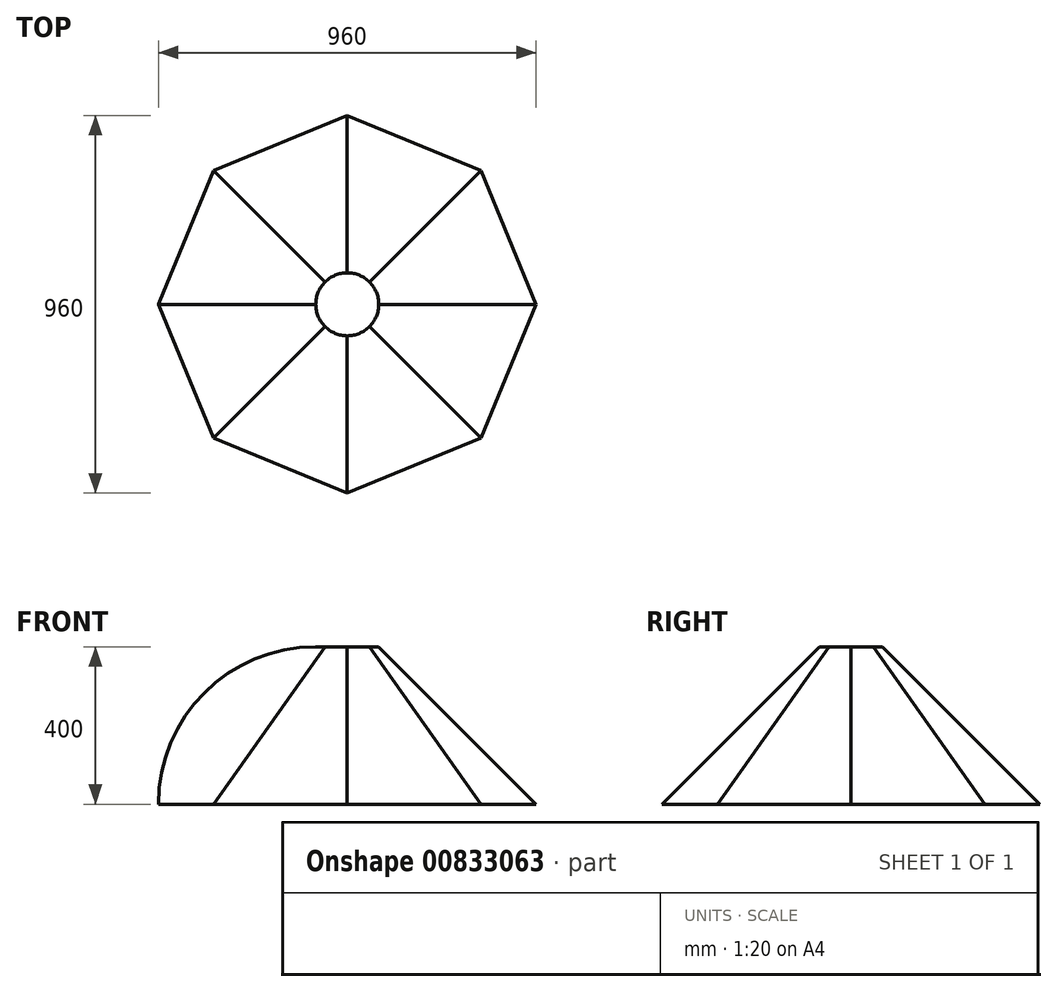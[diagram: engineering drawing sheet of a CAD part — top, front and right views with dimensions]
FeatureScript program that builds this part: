
annotation { "Feature Type Name" : "Feature", "Feature Type Description" : "" }
export const myFeature = defineFeature(function(context is Context, id is Id, definition is map)
    precondition{}
    {
        {
            var Q0;
            Q0=qCreatedBy(makeId("Top.planeOp"),FACE);
            cPlane(context, id + "F0", {"entities" : qUnion([Q0]), "cplaneType" : CPlaneType.OFFSET, "offset" : 400 * mm, "width" : 150 * mm, "height" : 150 * mm});
        }
        {
            var Q0;
            Q0=qCreatedBy(id+"F0.planeOp",FACE);
            var sketch = newSketch(context, id + "F1", { "sketchPlane" : qUnion([Q0])});
            skCircle(sketch, "E0", {"center": v(0, 0) * mm, "radius": 80 * mm});
            skSolve(sketch);
        }
        {
            var Q0;
            Q0=qCreatedBy(makeId("Top.planeOp"),FACE);
            var sketch = newSketch(context, id + "F2", { "sketchPlane" : qUnion([Q0])});
            skCircle(sketch, "E1.cCircle", {"center": v(0, 0) * mm, "radius": 443.46 * mm, "construction": true});
            skLineSegment(sketch, "E1.0", {"start": v(0, -480) * mm, "end": v(-339.41, -339.41) * mm});
            skLineSegment(sketch, "E1.1", {"start": v(-339.41, -339.41) * mm, "end": v(-480, 0) * mm});
            skLineSegment(sketch, "E1.2", {"start": v(-480, 0) * mm, "end": v(-339.41, 339.41) * mm});
            skLineSegment(sketch, "E1.3", {"start": v(-339.41, 339.41) * mm, "end": v(0, 480) * mm});
            skLineSegment(sketch, "E1.4", {"start": v(0, 480) * mm, "end": v(339.41, 339.41) * mm});
            skLineSegment(sketch, "E1.5", {"start": v(339.41, 339.41) * mm, "end": v(480, 0) * mm});
            skLineSegment(sketch, "E1.6", {"start": v(480, 0) * mm, "end": v(339.41, -339.41) * mm});
            skLineSegment(sketch, "E1.7", {"start": v(339.41, -339.41) * mm, "end": v(0, -480) * mm});
            skPoint(sketch, "E1.0.midPoint", {"position": v(-169.7, -409.7) * mm});
            skSolve(sketch);
        }
        {
            var Q0;
            Q0=qCreatedBy(makeId("Front.planeOp"),FACE);
            var sketch = newSketch(context, id + "F3", { "sketchPlane" : qUnion([Q0])});
            skLineSegment(sketch, "E2", {"start": v(0, 0) * mm, "end": v(-80, 0) * mm});
            skArc(sketch, "E3", {"start": v(-80, 400) * mm, "mid": v(-362.84, 282.84) * mm, "end": v(-480, 0) * mm});
            skSolve(sketch);
        }
        {
            var Q0;
            Q0=makeQuery(id+"F2.imprint","IMPRINT",FACE,{"disambiguationData":[TD([[makeQuery(id+"F2.imprint","IMPRINT",EDGE,{"derivedFrom":sQuery(id+"F2.wireOp",EDGE,"E1.0")}),-1.0]])]});
            var Q1;
            Q1=makeQuery(id+"F1.imprint","IMPRINT",FACE,{"disambiguationData":[TD([[makeQuery(id+"F1.imprint","IMPRINT",EDGE,{"derivedFrom":sQuery(id+"F1.wireOp",EDGE,"E0")}),1.0]])]});
            var Q2;
            Q2=sQuery(id+"F3.wireOp",EDGE,"E3");
            var Q3;
            Q3=sQuery(id+"FWh4wwSzDVeMAVq_0.7.F3.wireOp",EDGE,"E3");
            var Q4;
            Q4=sQuery(id+"FWh4wwSzDVeMAVq_0.6.F3.wireOp",EDGE,"E3");
            var Q5;
            Q5=sQuery(id+"FWh4wwSzDVeMAVq_0.5.F3.wireOp",EDGE,"E3");
            var Q6;
            Q6=sQuery(id+"FWh4wwSzDVeMAVq_0.4.F3.wireOp",EDGE,"E3");
            var Q7;
            Q7=sQuery(id+"FWh4wwSzDVeMAVq_0.3.F3.wireOp",EDGE,"E3");
            var Q8;
            Q8=sQuery(id+"FWh4wwSzDVeMAVq_0.2.F3.wireOp",EDGE,"E3");
            var Q9;
            Q9=sQuery(id+"FWh4wwSzDVeMAVq_0.1.F3.wireOp",EDGE,"E3");
            loft(context, id + "F4", {"addGuides" : true, "sheetProfilesArray" : [{ "sheetProfileEntities" : qUnion([Q0]) }, { "sheetProfileEntities" : qUnion([Q1]) }], "guidesArray" : [{ "guideEntities" : qUnion([Q2]), "guideDerivativeType" : LoftGuideDerivativeType.DEFAULT, "guideDerivativeMagnitude" : 1 }, { "guideEntities" : qUnion([Q3]), "guideDerivativeType" : LoftGuideDerivativeType.DEFAULT, "guideDerivativeMagnitude" : 1 }, { "guideEntities" : qUnion([Q4]), "guideDerivativeType" : LoftGuideDerivativeType.DEFAULT, "guideDerivativeMagnitude" : 1 }, { "guideEntities" : qUnion([Q5]), "guideDerivativeType" : LoftGuideDerivativeType.DEFAULT, "guideDerivativeMagnitude" : 1 }, { "guideEntities" : qUnion([Q6]), "guideDerivativeType" : LoftGuideDerivativeType.DEFAULT, "guideDerivativeMagnitude" : 1 }, { "guideEntities" : qUnion([Q7]), "guideDerivativeType" : LoftGuideDerivativeType.DEFAULT, "guideDerivativeMagnitude" : 1 }, { "guideEntities" : qUnion([Q8]), "guideDerivativeType" : LoftGuideDerivativeType.DEFAULT, "guideDerivativeMagnitude" : 1 }, { "guideEntities" : qUnion([Q9]), "guideDerivativeType" : LoftGuideDerivativeType.DEFAULT, "guideDerivativeMagnitude" : 1 }]});
        }
    });
